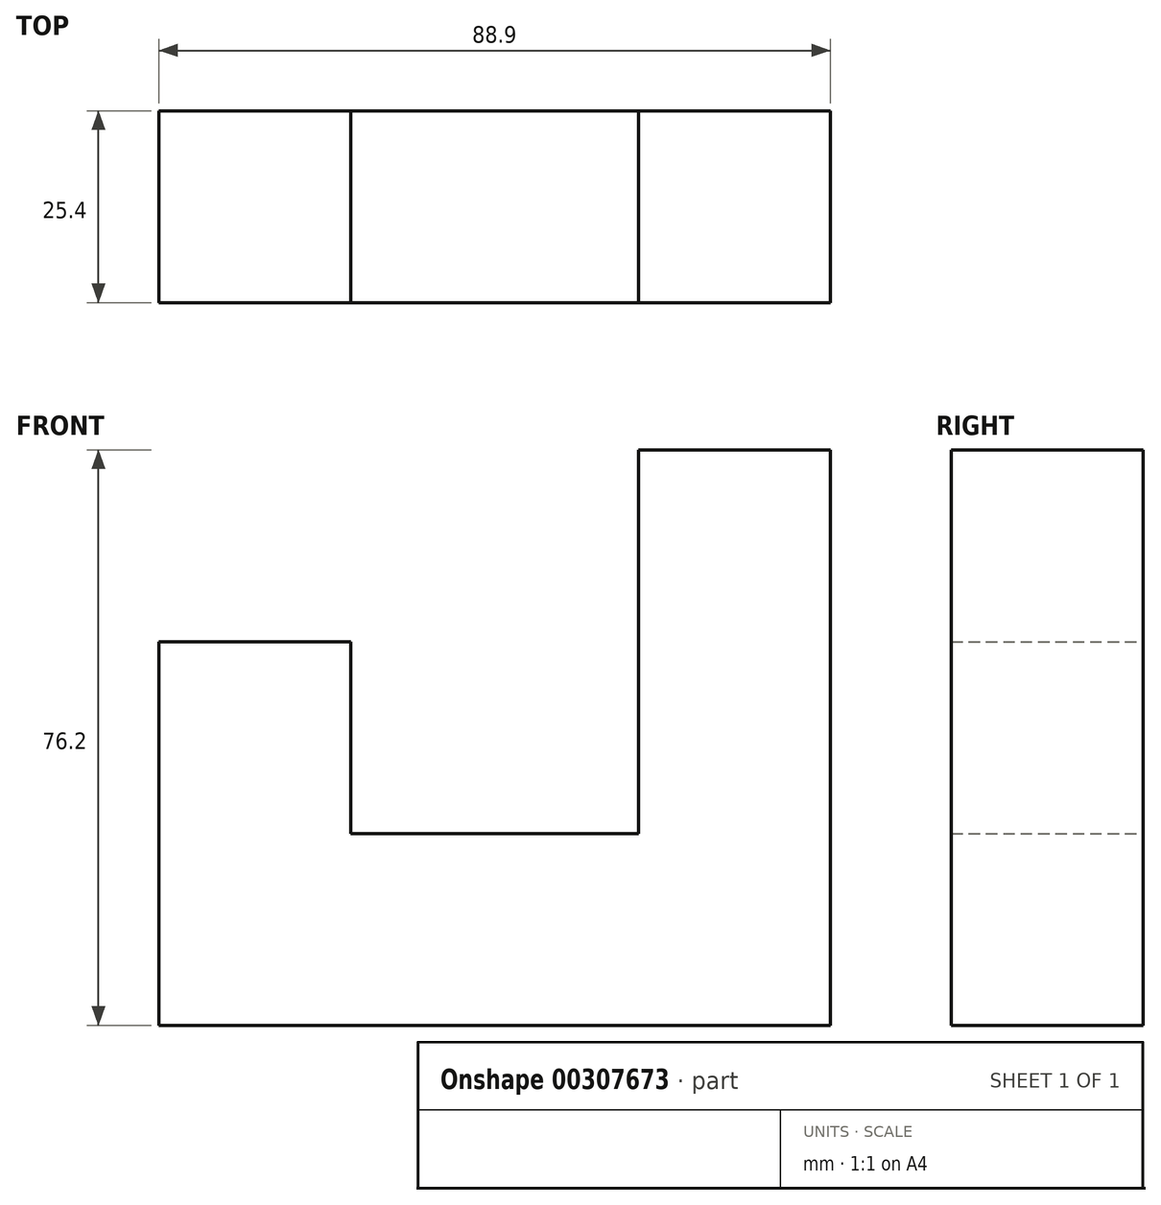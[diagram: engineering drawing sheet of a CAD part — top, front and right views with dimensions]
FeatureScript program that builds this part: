
annotation { "Feature Type Name" : "Feature", "Feature Type Description" : "" }
export const myFeature = defineFeature(function(context is Context, id is Id, definition is map)
    precondition{}
    {
        {
            var Q0;
            Q0=qCreatedBy(makeId("Front.planeOp"),FACE);
            var sketch = newSketch(context, id + "F0", { "sketchPlane" : qUnion([Q0])});
            skLineSegment(sketch, "E0", {"start": v(-46.37, -40.33) * mm, "end": v(42.53, -40.33) * mm});
            skLineSegment(sketch, "E1", {"start": v(42.53, -40.33) * mm, "end": v(42.53, 35.87) * mm});
            skLineSegment(sketch, "E2", {"start": v(42.53, 35.87) * mm, "end": v(17.13, 35.87) * mm});
            skLineSegment(sketch, "E3", {"start": v(17.13, 35.87) * mm, "end": v(17.13, -14.93) * mm});
            skLineSegment(sketch, "E4", {"start": v(17.13, -14.93) * mm, "end": v(-20.97, -14.93) * mm});
            skLineSegment(sketch, "E5", {"start": v(-20.97, -14.93) * mm, "end": v(-20.97, 10.47) * mm});
            skLineSegment(sketch, "E6", {"start": v(-20.97, 10.47) * mm, "end": v(-46.37, 10.47) * mm});
            skLineSegment(sketch, "E7", {"start": v(-46.37, 10.47) * mm, "end": v(-46.37, -40.33) * mm});
            skSolve(sketch);
        }
        {
            var Q0;
            Q0=makeQuery(id+"F0.imprint","IMPRINT",FACE,{"disambiguationData":[TD([[makeQuery(id+"F0.imprint","IMPRINT",EDGE,{"derivedFrom":sQuery(id+"F0.wireOp",EDGE,"E0")}),1.0]])]});
            extrude(context, id + "F1", {"entities" : qUnion([Q0]), "depth" : 25.4 * mm});
        }
    });
